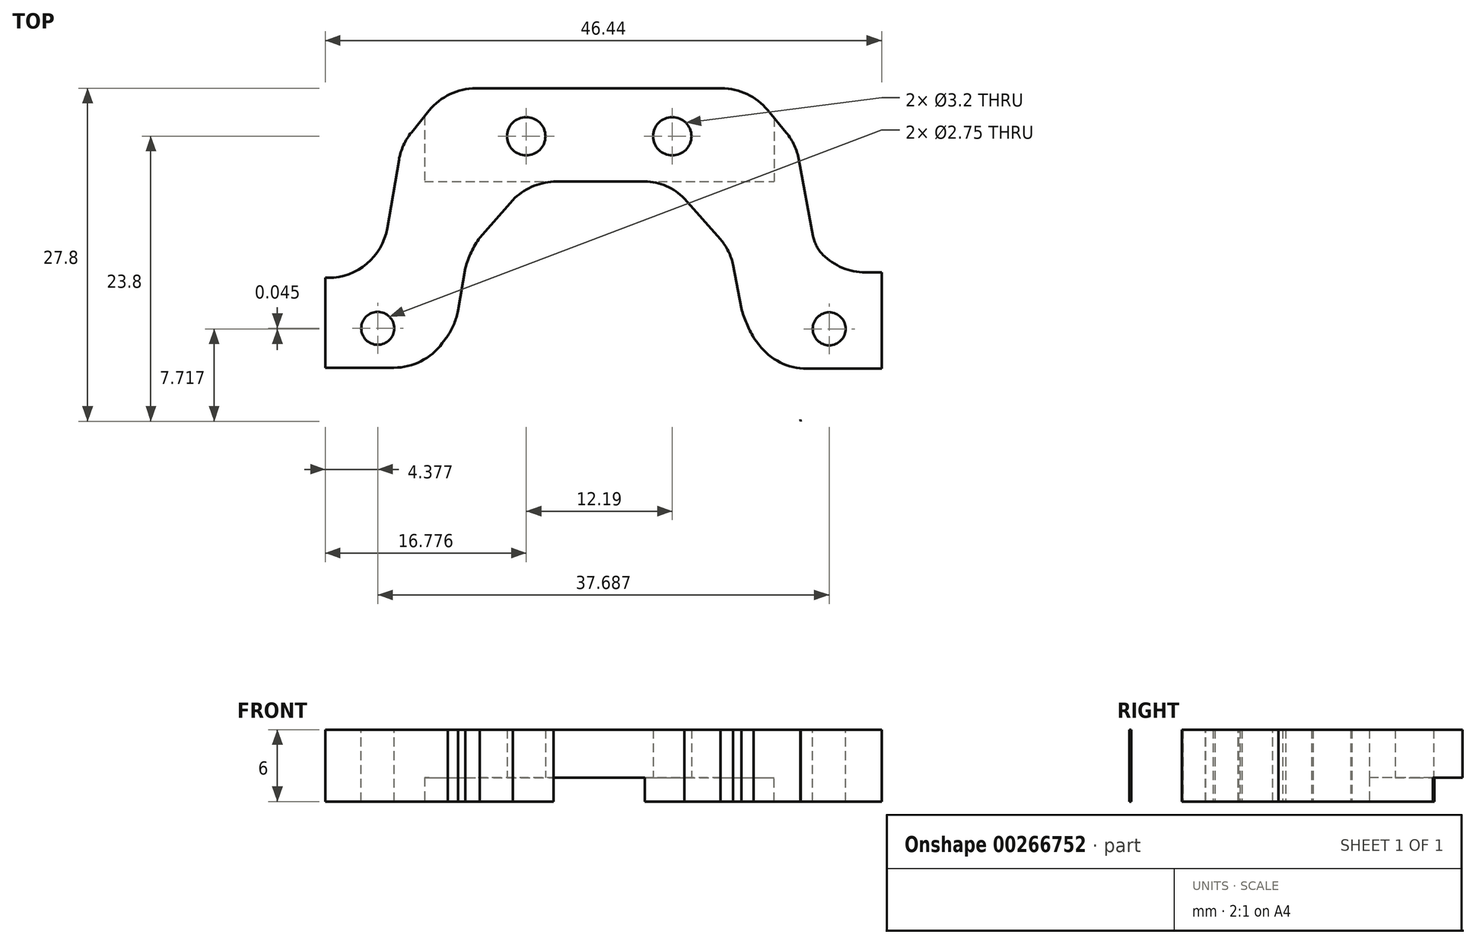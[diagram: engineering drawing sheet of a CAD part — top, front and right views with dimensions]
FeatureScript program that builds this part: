
annotation { "Feature Type Name" : "Feature", "Feature Type Description" : "" }
export const myFeature = defineFeature(function(context is Context, id is Id, definition is map)
    precondition{}
    {
        {
            var Q0;
            Q0=qCreatedBy(makeId("Top.planeOp"),FACE);
            var sketch = newSketch(context, id + "F0", { "sketchPlane" : qUnion([Q0])});
            skLineSegment(sketch, "E0.top", {"start": v(-35.25, 26) * mm, "end": v(-10, 26) * mm});
            skPoint(sketch, "E1.orphan", {"position": v(0, 26) * mm});
            skPoint(sketch, "E2.end.orphan", {"position": v(-5.25, 26) * mm});
            skPoint(sketch, "E3.end.orphan", {"position": v(-35.25, 26) * mm});
            skLineSegment(sketch, "E4", {"start": v(-39.06, 21.32) * mm, "end": v(-40.36, 13.78) * mm});
            skPoint(sketch, "E5.end.orphan", {"position": v(-38, 7.17) * mm});
            skLineSegment(sketch, "E6", {"start": v(-39.06, 21.32) * mm, "end": v(-35.25, 26) * mm});
            skPoint(sketch, "E7.orphan", {"position": v(-3.5, 7.17) * mm});
            skPoint(sketch, "E8.orphan", {"position": v(-7, 7.17) * mm});
            skLineSegment(sketch, "E9", {"start": v(-5.93, 20.23) * mm, "end": v(-4.58, 12.98) * mm});
            skPoint(sketch, "E10.start.orphan", {"position": v(-7, 26) * mm});
            skPoint(sketch, "E11.orphan", {"position": v(-38.25, 26) * mm});
            skLineSegment(sketch, "E12.right", {"start": v(6.6, 3.67) * mm, "end": v(6.6, 3.58) * mm});
            skLineSegment(sketch, "E13", {"start": v(-26.37, 18.22) * mm, "end": v(-18.77, 18.22) * mm});
            skLineSegment(sketch, "E14", {"start": v(-15.46, 16.79) * mm, "end": v(-12.45, 13.4) * mm});
            skLineSegment(sketch, "E15", {"start": v(-32.53, 13.54) * mm, "end": v(-29.78, 16.68) * mm});
            skLineSegment(sketch, "E16", {"start": v(-33.74, 11) * mm, "end": v(-34.35, 7.46) * mm});
            skLineSegment(sketch, "E17", {"start": v(-11.38, 11.25) * mm, "end": v(-10.7, 7.62) * mm});
            skLineSegment(sketch, "E18", {"start": v(-37.17, 2.67) * mm, "end": v(-35.2, 5.34) * mm});
            skLineSegment(sketch, "E19", {"start": v(-9.67, 5.18) * mm, "end": v(-7.72, 2.59) * mm});
            skPoint(sketch, "E20.orphan", {"position": v(-9.29, 0) * mm});
            skPoint(sketch, "E21.orphan", {"position": v(-35.63, 0) * mm});
            skArc(sketch, "E22", {"start": v(-41.85, 10.17) * mm, "mid": v(-40.84, 12.12) * mm, "end": v(-40.28, 14.24) * mm});
            skPoint(sketch, "E23.start.orphan", {"position": v(-45, 7.17) * mm});
            skArc(sketch, "E24", {"start": v(-4.71, 13.7) * mm, "mid": v(-4.66, 13.34) * mm, "end": v(-4.58, 12.98) * mm});
            skPoint(sketch, "E25.orphan", {"position": v(-41.5, 7.17) * mm});
            skPoint(sketch, "E26.orphan", {"position": v(0, 7.17) * mm});
            skArc(sketch, "E27", {"start": v(-32.53, 13.54) * mm, "mid": v(-33.24, 12.32) * mm, "end": v(-33.74, 11) * mm});
            skPoint(sketch, "E28.orphan", {"position": v(-33.48, 12.45) * mm});
            skArc(sketch, "E29", {"start": v(-26.37, 18.22) * mm, "mid": v(-28.22, 17.76) * mm, "end": v(-29.78, 16.68) * mm});
            skPoint(sketch, "E30.orphan", {"position": v(-28.43, 18.22) * mm});
            skArc(sketch, "E31", {"start": v(-15.46, 16.79) * mm, "mid": v(-16.97, 17.85) * mm, "end": v(-18.77, 18.22) * mm});
            skPoint(sketch, "E32.orphan", {"position": v(-16.74, 18.22) * mm});
            skArc(sketch, "E33", {"start": v(-11.32, 10.96) * mm, "mid": v(-11.71, 12.26) * mm, "end": v(-12.45, 13.4) * mm});
            skPoint(sketch, "E34.orphan", {"position": v(-11.6, 12.44) * mm});
            skArc(sketch, "E35", {"start": v(-10.7, 7.62) * mm, "mid": v(-10.26, 6.37) * mm, "end": v(-9.67, 5.18) * mm});
            skPoint(sketch, "E36.orphan", {"position": v(-10.44, 6.22) * mm});
            skArc(sketch, "E37", {"start": v(-35.2, 5.34) * mm, "mid": v(-34.67, 6.36) * mm, "end": v(-34.35, 7.46) * mm});
            skPoint(sketch, "E38.orphan", {"position": v(-34.56, 6.22) * mm});
            skArc(sketch, "E39", {"start": v(-7.73, 2.6) * mm, "mid": v(-7.73, 2.59) * mm, "end": v(-7.72, 2.59) * mm});
            skPoint(sketch, "E40.orphan", {"position": v(-5.79, 0) * mm});
            skPoint(sketch, "E41.orphan", {"position": v(-39.13, 0) * mm});
            skPoint(sketch, "E42.orphan", {"position": v(-51.5, 7.17) * mm});
            skArc(sketch, "E43", {"start": v(-5.78, -1.65) * mm, "mid": v(-5.76, -1.72) * mm, "end": v(-5.74, -1.8) * mm});
            skArc(sketch, "E44", {"start": v(-5.74, -1.8) * mm, "mid": v(-5.76, -1.72) * mm, "end": v(-5.78, -1.65) * mm});
            skPoint(sketch, "E45.orphan", {"position": v(-1.68, -4.07) * mm});
            skPoint(sketch, "E46.orphan", {"position": v(-41.5, -4.07) * mm});
            skPoint(sketch, "E47.orphan", {"position": v(-43.22, -4.07) * mm});
            skArc(sketch, "E48", {"start": v(6.6, 3.58) * mm, "mid": v(6.6, 3.63) * mm, "end": v(6.61, 3.67) * mm});
            skPoint(sketch, "E49.orphan", {"position": v(6.5, 7.17) * mm});
            skPoint(sketch, "E50.centerSnap0", {"position": v(-51.6, 2.1) * mm});
            skLineSegment(sketch, "E51", {"start": v(-5.93, 20.23) * mm, "end": v(-6.14, 21.32) * mm});
            skLineSegment(sketch, "E52", {"start": v(-6.14, 21.32) * mm, "end": v(-10, 26) * mm});
            skPoint(sketch, "E53.end.orphan", {"position": v(-5.88, 21.32) * mm});
            skPoint(sketch, "E54.orphan", {"position": v(-44.94, -4.07) * mm});
            skPoint(sketch, "E0.bottom.start.orphan", {"position": v(-44.94, 0) * mm});
            skPoint(sketch, "E55.top.end.orphan", {"position": v(-51.63, 0) * mm});
            skPoint(sketch, "E12.top.start.orphan", {"position": v(0, 0) * mm});
            skPoint(sketch, "E56.trimOffspring.start.orphan", {"position": v(-3.36, 0) * mm});
            skPoint(sketch, "E57.orphan", {"position": v(-3.36, -4.07) * mm});
            skPoint(sketch, "E58.end.orphan", {"position": v(6.71, 0) * mm});
            skPoint(sketch, "E58.start.orphan", {"position": v(0, -4.07) * mm});
            skArc(sketch, "E59", {"start": v(-50.32, 1.28) * mm, "mid": v(-50.02, 0.97) * mm, "end": v(-49.7, 0.67) * mm});
            skPoint(sketch, "E60.centerSnap0", {"position": v(-43.93, 0.67) * mm});
            skPoint(sketch, "E61.centerSnap0", {"position": v(-0.52, 0.67) * mm});
            skPoint(sketch, "E61.perimeterSnap0", {"position": v(-0.52, 0.67) * mm});
            skPoint(sketch, "E61.perimeterSnap1", {"position": v(-36.19, 4) * mm});
            skPoint(sketch, "E62.orphan", {"position": v(4.33, -0.8) * mm});
            skPoint(sketch, "E63.start.orphan", {"position": v(-49.7, 0.67) * mm});
            skLineSegment(sketch, "E64.trimOffspring", {"start": v(6.58, 3.67) * mm, "end": v(6.61, 3.67) * mm});
            skArc(sketch, "E65", {"start": v(-51.04, 2.69) * mm, "mid": v(-50.75, 1.95) * mm, "end": v(-50.32, 1.28) * mm});
            skPoint(sketch, "E55.right.end.orphan", {"position": v(-51.57, 3.58) * mm});
            skPoint(sketch, "E55.right.start.orphan", {"position": v(-51.56, 4.2) * mm});
            skArc(sketch, "E66", {"start": v(-4.58, 12.98) * mm, "mid": v(-3.94, 11.76) * mm, "end": v(-3.14, 10.63) * mm});
            skLineSegment(sketch, "E67.top", {"start": v(-51.04, 10.17) * mm, "end": v(-41.85, 10.17) * mm});
            skLineSegment(sketch, "E67.left", {"start": v(-51.04, 4.83) * mm, "end": v(-51.04, 10.17) * mm});
            skPoint(sketch, "E68.center.orphan", {"position": v(-43.93, 3.67) * mm});
            skLineSegment(sketch, "E69", {"start": v(-51.04, 4.83) * mm, "end": v(-51.04, 2.69) * mm});
            skLineSegment(sketch, "E70", {"start": v(-51.04, 2.69) * mm, "end": v(-37.17, 2.67) * mm});
            skLineSegment(sketch, "E71", {"start": v(-7.72, 2.59) * mm, "end": v(6.73, 2.59) * mm});
            skPoint(sketch, "E72.center.orphan", {"position": v(-0.52, 3.67) * mm});
            skLineSegment(sketch, "E73.bottom", {"start": v(-3.14, 10.63) * mm, "end": v(6.61, 10.63) * mm});
            skLineSegment(sketch, "E73.right", {"start": v(6.61, 10.63) * mm, "end": v(6.61, 4.69) * mm});
            skPoint(sketch, "E74.orphan", {"position": v(3.25, 7.17) * mm});
            skPoint(sketch, "E75.orphan", {"position": v(5.62, 0.67) * mm});
            skPoint(sketch, "E76.trimOffspring.start.orphan", {"position": v(-6.65, 0.67) * mm});
            skLineSegment(sketch, "E77", {"start": v(6.61, 4.69) * mm, "end": v(6.61, 2.59) * mm});
            skPoint(sketch, "E78.end.orphan", {"position": v(-38.17, 0.67) * mm});
            skSolve(sketch);
        }
        {
            var Q0;
            Q0=qSketchRegion(id+"F0",true);
            extrude(context, id + "F1", {"entities" : qUnion([Q0]), "depth" : 6 * mm});
        }
        {
            var Q0;
            Q0=makeQuery(id+"F1.opExtrude","CAP_FACE",FACE,{"disambiguationData":[OSD([sQuery(id+"F0.wireOp",EDGE,"E0.top"),sQuery(id+"F0.wireOp",EDGE,"E4"),sQuery(id+"F0.wireOp",EDGE,"E6"),sQuery(id+"F0.wireOp",EDGE,"dBJT8Cw2-kiiE-JVtB-cWXl-Jo8WRkg6q42H"),sQuery(id+"F0.wireOp",EDGE,"E9"),sQuery(id+"F0.wireOp",EDGE,"E55.right"),sQuery(id+"F0.wireOp",EDGE,"E12.right"),sQuery(id+"F0.wireOp",EDGE,"E13"),sQuery(id+"F0.wireOp",EDGE,"E14"),sQuery(id+"F0.wireOp",EDGE,"E15"),sQuery(id+"F0.wireOp",EDGE,"E16"),sQuery(id+"F0.wireOp",EDGE,"E17"),sQuery(id+"F0.wireOp",EDGE,"E18"),sQuery(id+"F0.wireOp",EDGE,"E19"),sQuery(id+"F0.wireOp",EDGE,"E22"),sQuery(id+"F0.wireOp",EDGE,"E24"),sQuery(id+"F0.wireOp",EDGE,"rj1mGid4-xFnT-5L7G-8oH3-5rQVDscBIdu8"),sQuery(id+"F0.wireOp",EDGE,"ebojeOF5-0V5Z-GACH-SJHX-2aT5HY6FHZ65"),sQuery(id+"F0.wireOp",EDGE,"E27"),sQuery(id+"F0.wireOp",EDGE,"E29"),sQuery(id+"F0.wireOp",EDGE,"E31"),sQuery(id+"F0.wireOp",EDGE,"E33"),sQuery(id+"F0.wireOp",EDGE,"E35"),sQuery(id+"F0.wireOp",EDGE,"E37"),sQuery(id+"F0.wireOp",EDGE,"E39"),sQuery(id+"F0.wireOp",EDGE,"7pML4YSL-yiDA-D2yh-V960-KRGg61vCjFmG"),sQuery(id+"F0.wireOp",EDGE,"IGeuu9I0-9ooR-3LEY-gD5L-lz7DSk6ZP3Wm"),sQuery(id+"F0.wireOp",EDGE,"ArIczMb2-31dy-rm4w-YmVm-JGPmwflz5pzP"),sQuery(id+"F0.wireOp",EDGE,"E43"),sQuery(id+"F0.wireOp",EDGE,"5CBCV5pV-P6g0-NZko-TJbt-ypDVxmAhKuvs"),sQuery(id+"F0.wireOp",EDGE,"E44"),sQuery(id+"F0.wireOp",EDGE,"E78"),sQuery(id+"F0.wireOp",EDGE,"E48"),sQuery(id+"F0.wireOp",EDGE,"E58"),sQuery(id+"F0.wireOp",EDGE,"0UirUm4J-w40v-Yv3M-HN0D-oRn1FItKkyv0")])],"isStart":true});
            var sketch = newSketch(context, id + "F2", { "sketchPlane" : qUnion([Q0])});
            skPoint(sketch, "E79.firstSnap0", {"position": v(-37.15, -23.66) * mm});
            skPoint(sketch, "E79.oppositeSnap0", {"position": v(-7.96, -23.12) * mm});
            skLineSegment(sketch, "E79.bottom", {"start": v(-37.15, -26.33) * mm, "end": v(-7.96, -26.33) * mm});
            skLineSegment(sketch, "E79.left", {"start": v(-37.15, -26.33) * mm, "end": v(-37.15, -18.22) * mm});
            skLineSegment(sketch, "E79.right", {"start": v(-7.96, -26.33) * mm, "end": v(-7.96, -18.22) * mm});
            skLineSegment(sketch, "E80", {"start": v(-37.15, -18.22) * mm, "end": v(-7.96, -18.22) * mm});
            skPoint(sketch, "E81.orphan", {"position": v(-7.96, -14.58) * mm});
            skSolve(sketch);
        }
        {
            var Q0;
            Q0=qSketchRegion(id+"F2",true);
            extrude(context, id + "F3", {"entities" : qUnion([Q0]), "operationType" : NewBodyOperationType.REMOVE, "oppositeDirection" : true, "depth" : 2 * mm});
        }
        {
            var Q0;
            Q0=makeQuery(id+"F3.boolean.opBoolean","COPY",FACE,{"derivedFrom":makeQuery(id+"F3.opExtrude","CAP_FACE",FACE,{"disambiguationData":[OSD([sQuery(id+"F2.wireOp",EDGE,"E79.bottom"),sQuery(id+"F2.wireOp",EDGE,"E79.top"),sQuery(id+"F2.wireOp",EDGE,"E79.left"),sQuery(id+"F2.wireOp",EDGE,"E79.right")])],"isStart":false})});
            var sketch = newSketch(context, id + "F4", { "sketchPlane" : qUnion([Q0])});
            skCircle(sketch, "E82", {"center": v(-28.65, -22) * mm, "radius": 1.6 * mm});
            skCircle(sketch, "E83", {"center": v(-16.46, -22) * mm, "radius": 1.6 * mm});
            skSolve(sketch);
        }
        {
            var Q0;
            Q0=qSketchRegion(id+"F4",true);
            extrude(context, id + "F5", {"entities" : qUnion([Q0]), "operationType" : NewBodyOperationType.REMOVE, "oppositeDirection" : true, "depth" : 25 * mm});
        }
        {
            var Q0;
            Q0=makeQuery(id+"F1.opExtrude","SWEPT_EDGE",EDGE,{"disambiguationData":[OSD([sQuery(id+"F0.wireOp",EDGE,"E69"),sQuery(id+"F0.wireOp",EDGE,"E70")])]});
            var Q1;
            Q1=makeQuery(id+"F1.opExtrude","SWEPT_EDGE",EDGE,{"disambiguationData":[OSD([sQuery(id+"F0.wireOp",EDGE,"E67.top"),sQuery(id+"F0.wireOp",EDGE,"E67.left")])]});
            var Q2;
            Q2=makeQuery(id+"F1.opExtrude","SWEPT_EDGE",EDGE,{"disambiguationData":[OSD([sQuery(id+"F0.wireOp",EDGE,"E71"),sQuery(id+"F0.wireOp",EDGE,"E77")])]});
            var Q3;
            Q3=makeQuery(id+"F1.opExtrude","SWEPT_EDGE",EDGE,{"disambiguationData":[OSD([sQuery(id+"F0.wireOp",EDGE,"E73.bottom"),sQuery(id+"F0.wireOp",EDGE,"E73.right")])]});
            fillet(context, id + "F6", {"entities" : qUnion([Q0, Q1, Q2, Q3]), "radius" : 3 * mm, "tangentPropagation" : true, "allowEdgeOverflow" : false});
        }
        {
            var Q0;
            Q0=makeQuery(id+"F1.opExtrude","SWEPT_EDGE",EDGE,{"disambiguationData":[OSD([sQuery(id+"F0.wireOp",EDGE,"E39"),sQuery(id+"F0.wireOp",EDGE,"E71")])]});
            var Q1;
            Q1=makeQuery(id+"F1.opExtrude","SWEPT_EDGE",EDGE,{"disambiguationData":[OSD([sQuery(id+"F0.wireOp",EDGE,"E18"),sQuery(id+"F0.wireOp",EDGE,"E70")])]});
            fillet(context, id + "F7", {"entities" : qUnion([Q0, Q1]), "radius" : 5 * mm, "tangentPropagation" : true, "allowEdgeOverflow" : false});
        }
        {
            var Q0;
            Q0=makeQuery(id+"F1.opExtrude","SWEPT_EDGE",EDGE,{"disambiguationData":[OSD([sQuery(id+"F0.wireOp",EDGE,"E22"),sQuery(id+"F0.wireOp",EDGE,"E67.top")])]});
            var Q1;
            Q1=makeQuery(id+"F1.opExtrude","SWEPT_EDGE",EDGE,{"disambiguationData":[OSD([sQuery(id+"F0.wireOp",EDGE,"E66"),sQuery(id+"F0.wireOp",EDGE,"E73.bottom")])]});
            fillet(context, id + "F8", {"entities" : qUnion([Q0, Q1]), "radius" : 5 * mm, "tangentPropagation" : true, "allowEdgeOverflow" : false});
        }
        {
            var Q0;
            Q0=makeQuery(id+"F1.opExtrude","CAP_FACE",FACE,{"disambiguationData":[OSD([sQuery(id+"F0.wireOp",EDGE,"E0.top"),sQuery(id+"F0.wireOp",EDGE,"E4"),sQuery(id+"F0.wireOp",EDGE,"E6"),sQuery(id+"F0.wireOp",EDGE,"E9"),sQuery(id+"F0.wireOp",EDGE,"E13"),sQuery(id+"F0.wireOp",EDGE,"E14"),sQuery(id+"F0.wireOp",EDGE,"E15"),sQuery(id+"F0.wireOp",EDGE,"E16"),sQuery(id+"F0.wireOp",EDGE,"E17"),sQuery(id+"F0.wireOp",EDGE,"E18"),sQuery(id+"F0.wireOp",EDGE,"E19"),sQuery(id+"F0.wireOp",EDGE,"E22"),sQuery(id+"F0.wireOp",EDGE,"E27"),sQuery(id+"F0.wireOp",EDGE,"E29"),sQuery(id+"F0.wireOp",EDGE,"E31"),sQuery(id+"F0.wireOp",EDGE,"E33"),sQuery(id+"F0.wireOp",EDGE,"E35"),sQuery(id+"F0.wireOp",EDGE,"E37"),sQuery(id+"F0.wireOp",EDGE,"E39"),sQuery(id+"F0.wireOp",EDGE,"E51"),sQuery(id+"F0.wireOp",EDGE,"E52"),sQuery(id+"F0.wireOp",EDGE,"E66"),sQuery(id+"F0.wireOp",EDGE,"E67.top"),sQuery(id+"F0.wireOp",EDGE,"E67.left"),sQuery(id+"F0.wireOp",EDGE,"E69"),sQuery(id+"F0.wireOp",EDGE,"E70"),sQuery(id+"F0.wireOp",EDGE,"E71"),sQuery(id+"F0.wireOp",EDGE,"E73.bottom"),sQuery(id+"F0.wireOp",EDGE,"E73.right"),sQuery(id+"F0.wireOp",EDGE,"E77")])],"isStart":false});
            var sketch = newSketch(context, id + "F9", { "sketchPlane" : qUnion([Q0])});
            skCircle(sketch, "E84", {"center": v(-41.05, 5.96) * mm, "radius": 1.38 * mm});
            skPoint(sketch, "E84.centerSnap0", {"position": v(-41.05, 2.46) * mm});
            skCircle(sketch, "E85", {"center": v(-3.37, 5.92) * mm, "radius": 1.38 * mm});
            skPoint(sketch, "E85.centerSnap0", {"position": v(-3.37, 2.42) * mm});
            skSolve(sketch);
        }
        {
            var Q0;
            Q0=makeQuery(id+"F9.imprint","IMPRINT",FACE,{"disambiguationData":[TD([[makeQuery(id+"F9.imprint","IMPRINT",EDGE,{"derivedFrom":sQuery(id+"F9.wireOp",EDGE,"E84")}),1.0]])]});
            var Q1;
            Q1=makeQuery(id+"F9.imprint","IMPRINT",FACE,{"disambiguationData":[TD([[makeQuery(id+"F9.imprint","IMPRINT",EDGE,{"derivedFrom":sQuery(id+"F9.wireOp",EDGE,"E85")}),1.0]])]});
            extrude(context, id + "F10", {"entities" : qUnion([Q0, Q1]), "operationType" : NewBodyOperationType.REMOVE, "oppositeDirection" : true, "depth" : 25 * mm});
        }
        {
            var Q0;
            Q0=makeQuery(id+"F1.opExtrude","CAP_FACE",FACE,{"disambiguationData":[OSD([sQuery(id+"F0.wireOp",EDGE,"E0.top"),sQuery(id+"F0.wireOp",EDGE,"E4"),sQuery(id+"F0.wireOp",EDGE,"E6"),sQuery(id+"F0.wireOp",EDGE,"E9"),sQuery(id+"F0.wireOp",EDGE,"E13"),sQuery(id+"F0.wireOp",EDGE,"E14"),sQuery(id+"F0.wireOp",EDGE,"E15"),sQuery(id+"F0.wireOp",EDGE,"E16"),sQuery(id+"F0.wireOp",EDGE,"E17"),sQuery(id+"F0.wireOp",EDGE,"E18"),sQuery(id+"F0.wireOp",EDGE,"E19"),sQuery(id+"F0.wireOp",EDGE,"E22"),sQuery(id+"F0.wireOp",EDGE,"E27"),sQuery(id+"F0.wireOp",EDGE,"E29"),sQuery(id+"F0.wireOp",EDGE,"E31"),sQuery(id+"F0.wireOp",EDGE,"E33"),sQuery(id+"F0.wireOp",EDGE,"E35"),sQuery(id+"F0.wireOp",EDGE,"E37"),sQuery(id+"F0.wireOp",EDGE,"E39"),sQuery(id+"F0.wireOp",EDGE,"E51"),sQuery(id+"F0.wireOp",EDGE,"E52"),sQuery(id+"F0.wireOp",EDGE,"E66"),sQuery(id+"F0.wireOp",EDGE,"E67.top"),sQuery(id+"F0.wireOp",EDGE,"E67.left"),sQuery(id+"F0.wireOp",EDGE,"E69"),sQuery(id+"F0.wireOp",EDGE,"E70"),sQuery(id+"F0.wireOp",EDGE,"E71"),sQuery(id+"F0.wireOp",EDGE,"E73.bottom"),sQuery(id+"F0.wireOp",EDGE,"E73.right"),sQuery(id+"F0.wireOp",EDGE,"E77")])],"isStart":false});
            var sketch = newSketch(context, id + "F11", { "sketchPlane" : qUnion([Q0])});
            skLineSegment(sketch, "E86", {"start": v(-45.43, 10.17) * mm, "end": v(-45.43, 2.68) * mm});
            skLineSegment(sketch, "E87", {"start": v(1, 2.59) * mm, "end": v(1, 10.63) * mm});
            skSolve(sketch);
        }
        {
            var Q0;
            {var subQ7=sQuery(id+"F11.wireOp",EDGE,"E86");Q0=makeQuery(id+"F11.imprint","IMPRINT",FACE,{"disambiguationData":[TD([[makeQuery(id+"F11.imprint","IMPRINT",EDGE,{"derivedFrom":subQ7}),-1.0]])]});}
            var Q1;
            {var subQ6=sQuery(id+"F11.wireOp",EDGE,"E87");Q1=makeQuery(id+"F11.imprint","IMPRINT",FACE,{"disambiguationData":[TD([[makeQuery(id+"F11.imprint","IMPRINT",EDGE,{"derivedFrom":subQ6}),-1.0]])]});}
            extrude(context, id + "F12", {"entities" : qUnion([Q0, Q1]), "operationType" : NewBodyOperationType.REMOVE, "oppositeDirection" : true, "depth" : 25 * mm});
        }
        {
            var Q0;
            Q0=makeQuery(id+"F12.boolean.opBoolean","COPY",EDGE,{"derivedFrom":makeQuery(id+"F12.opExtrude","SWEPT_EDGE",EDGE,{"disambiguationData":[OSD([sQuery(id+"F0.wireOp",EDGE,"E70"),sQuery(id+"F11.wireOp",EDGE,"E86")])]})});
            var Q1;
            Q1=makeQuery(id+"F12.boolean.opBoolean","COPY",EDGE,{"derivedFrom":makeQuery(id+"F12.opExtrude","SWEPT_EDGE",EDGE,{"disambiguationData":[OSD([sQuery(id+"F0.wireOp",EDGE,"E67.top"),sQuery(id+"F11.wireOp",EDGE,"E86")])]})});
            var Q2;
            Q2=makeQuery(id+"F12.boolean.opBoolean","COPY",EDGE,{"derivedFrom":makeQuery(id+"F12.opExtrude","SWEPT_EDGE",EDGE,{"disambiguationData":[OSD([sQuery(id+"F0.wireOp",EDGE,"E71"),sQuery(id+"F11.wireOp",EDGE,"E87")])]})});
            var Q3;
            Q3=makeQuery(id+"F12.boolean.opBoolean","COPY",EDGE,{"derivedFrom":makeQuery(id+"F12.opExtrude","SWEPT_EDGE",EDGE,{"disambiguationData":[OSD([sQuery(id+"F0.wireOp",EDGE,"E73.bottom"),sQuery(id+"F11.wireOp",EDGE,"E87")])]})});
            var Q4;
            Q4=makeQuery(id+"F8.opFillet","BLEND_EDGE",EDGE,{"blendedFrom":[makeQuery(id+"F1.opExtrude","SWEPT_EDGE",EDGE,{"disambiguationData":[OSD([sQuery(id+"F0.wireOp",EDGE,"E66"),sQuery(id+"F0.wireOp",EDGE,"E73.bottom")])]}),makeQuery(id+"F1.opExtrude","SWEPT_FACE",FACE,{"disambiguationData":[OSD([sQuery(id+"F0.wireOp",EDGE,"E9")])]})],"blendedInto":[makeQuery(id+"F1.opExtrude","SWEPT_FACE",FACE,{"disambiguationData":[OSD([sQuery(id+"F0.wireOp",EDGE,"E9")])]})]});
            fillet(context, id + "F13", {"entities" : qUnion([Q0, Q1, Q2, Q3, Q4]), "radius" : 3 * mm, "tangentPropagation" : true, "allowEdgeOverflow" : false});
        }
        {
            var Q0;
            Q0=makeQuery(id+"F1.opExtrude","SWEPT_EDGE",EDGE,{"disambiguationData":[OSD([sQuery(id+"F0.wireOp",EDGE,"E4"),sQuery(id+"F0.wireOp",EDGE,"E6")])]});
            var Q1;
            Q1=makeQuery(id+"F1.opExtrude","SWEPT_EDGE",EDGE,{"disambiguationData":[OSD([sQuery(id+"F0.wireOp",EDGE,"E0.top"),sQuery(id+"F0.wireOp",EDGE,"E52")])]});
            var Q2;
            Q2=makeQuery(id+"F1.opExtrude","SWEPT_EDGE",EDGE,{"disambiguationData":[OSD([sQuery(id+"F0.wireOp",EDGE,"E51"),sQuery(id+"F0.wireOp",EDGE,"E52")])]});
            var Q3;
            Q3=makeQuery(id+"F1.opExtrude","SWEPT_EDGE",EDGE,{"disambiguationData":[OSD([sQuery(id+"F0.wireOp",EDGE,"E0.top"),sQuery(id+"F0.wireOp",EDGE,"E6")])]});
            fillet(context, id + "F14", {"entities" : qUnion([Q0, Q1, Q2, Q3]), "radius" : 5 * mm, "tangentPropagation" : true, "allowEdgeOverflow" : false});
        }
    });
